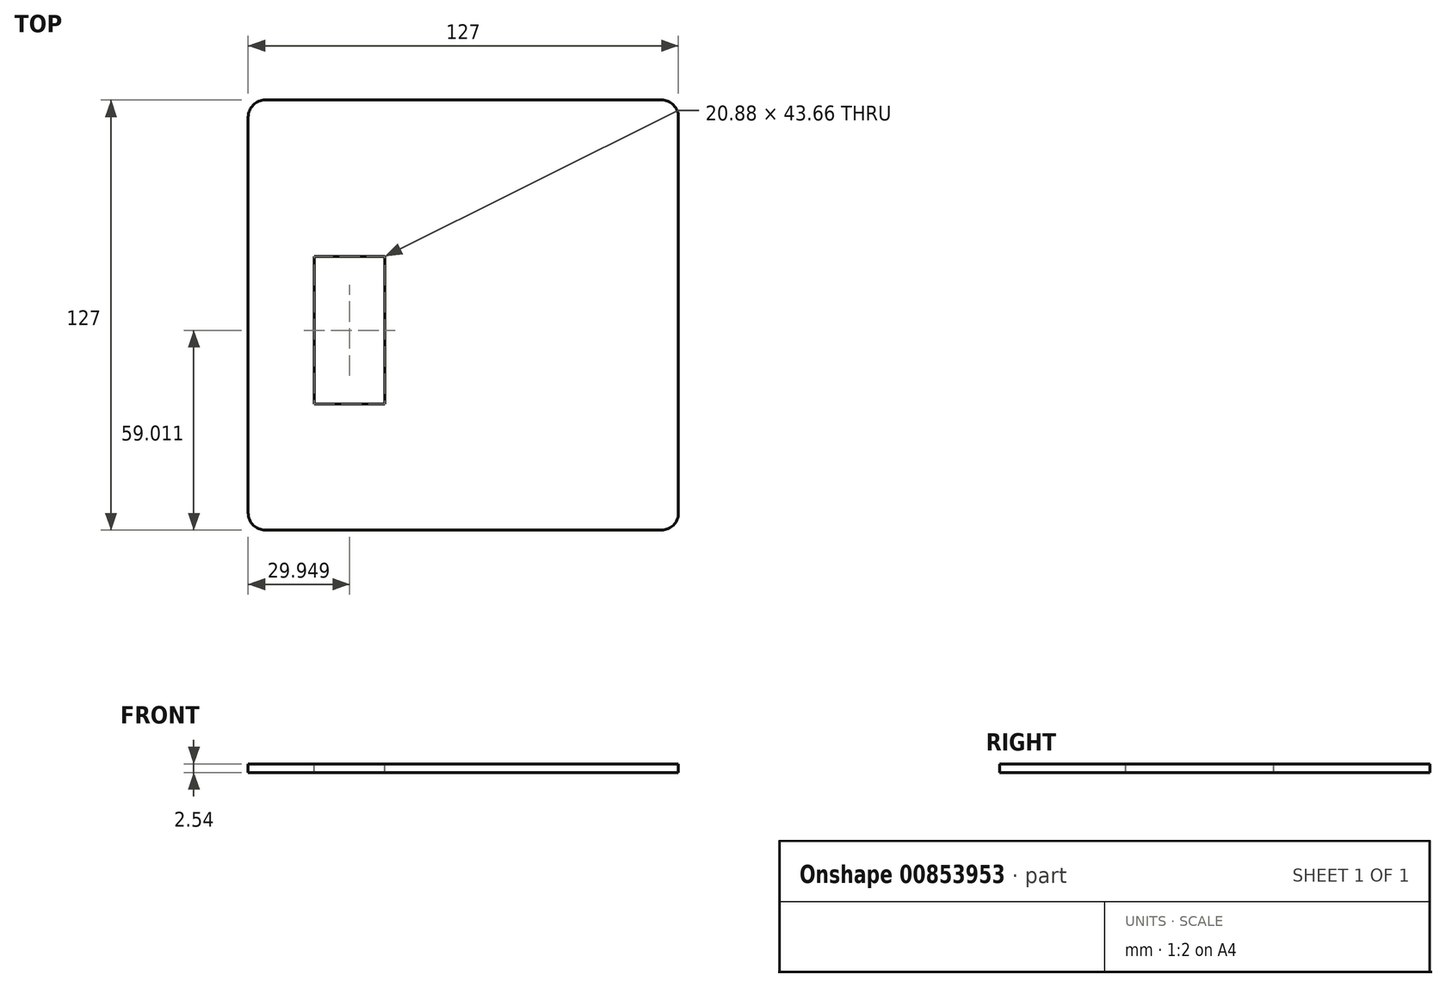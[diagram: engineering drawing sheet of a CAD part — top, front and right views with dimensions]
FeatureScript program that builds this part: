
annotation { "Feature Type Name" : "Feature", "Feature Type Description" : "" }
export const myFeature = defineFeature(function(context is Context, id is Id, definition is map)
    precondition{}
    {
        {
            var Q0;
            Q0=qCreatedBy(makeId("Top.planeOp"),FACE);
            var sketch = newSketch(context, id + "F0", { "sketchPlane" : qUnion([Q0])});
            skLineSegment(sketch, "E0.bottom", {"start": v(63.5, 63.5) * mm, "end": v(-63.5, 63.5) * mm});
            skLineSegment(sketch, "E0.top", {"start": v(63.5, -63.5) * mm, "end": v(-63.5, -63.5) * mm});
            skLineSegment(sketch, "E0.left", {"start": v(63.5, 63.5) * mm, "end": v(63.5, -63.5) * mm});
            skLineSegment(sketch, "E0.right", {"start": v(-63.5, 63.5) * mm, "end": v(-63.5, -63.5) * mm});
            skPoint(sketch, "E0.middle", {"position": v(0, 0) * mm});
            skSolve(sketch);
        }
        {
            var Q0;
            Q0=makeQuery(id+"F0.imprint","IMPRINT",FACE,{"disambiguationData":[TD([[makeQuery(id+"F0.imprint","IMPRINT",EDGE,{"derivedFrom":sQuery(id+"F0.wireOp",EDGE,"E0.bottom")}),1.0]])]});
            extrude(context, id + "F1", {"entities" : qUnion([Q0]), "depth" : 2.54 * mm, "offsetDistance" : 25.4 * mm});
        }
        {
            var Q0;
            Q0=makeQuery(id+"F1.opExtrude","SWEPT_EDGE",EDGE,{"disambiguationData":[OSD([sQuery(id+"F0.wireOp",EDGE,"E0.top"),sQuery(id+"F0.wireOp",EDGE,"E0.left")])]});
            var Q1;
            Q1=makeQuery(id+"F1.opExtrude","SWEPT_EDGE",EDGE,{"disambiguationData":[OSD([sQuery(id+"F0.wireOp",EDGE,"E0.bottom"),sQuery(id+"F0.wireOp",EDGE,"E0.left")])]});
            var Q2;
            Q2=makeQuery(id+"F1.opExtrude","SWEPT_EDGE",EDGE,{"disambiguationData":[OSD([sQuery(id+"F0.wireOp",EDGE,"E0.bottom"),sQuery(id+"F0.wireOp",EDGE,"E0.right")])]});
            var Q3;
            Q3=makeQuery(id+"F1.opExtrude","SWEPT_EDGE",EDGE,{"disambiguationData":[OSD([sQuery(id+"F0.wireOp",EDGE,"E0.top"),sQuery(id+"F0.wireOp",EDGE,"E0.right")])]});
            fillet(context, id + "F2", {"entities" : qUnion([Q0, Q1, Q2, Q3]), "radius" : 5.08 * mm, "tangentPropagation" : true, "allowEdgeOverflow" : false});
        }
        {
            var Q0;
            Q0=makeQuery(id+"F1.opExtrude","CAP_FACE",FACE,{"disambiguationData":[OSD([sQuery(id+"F0.wireOp",EDGE,"E0.bottom"),sQuery(id+"F0.wireOp",EDGE,"E0.top"),sQuery(id+"F0.wireOp",EDGE,"E0.left"),sQuery(id+"F0.wireOp",EDGE,"E0.right")])],"isStart":false});
            var sketch = newSketch(context, id + "F3", { "sketchPlane" : qUnion([Q0])});
            skLineSegment(sketch, "E1.bottom", {"start": v(-44, -26.32) * mm, "end": v(-23.1, -26.32) * mm});
            skLineSegment(sketch, "E1.top", {"start": v(-44, 17.34) * mm, "end": v(-23.1, 17.34) * mm});
            skLineSegment(sketch, "E1.left", {"start": v(-44, -26.32) * mm, "end": v(-44, 17.34) * mm});
            skLineSegment(sketch, "E1.right", {"start": v(-23.1, -26.32) * mm, "end": v(-23.1, 17.34) * mm});
            skSolve(sketch);
        }
        {
            var Q0;
            Q0=makeQuery(id+"F3.imprint","IMPRINT",FACE,{"disambiguationData":[TD([[makeQuery(id+"F3.imprint","IMPRINT",EDGE,{"derivedFrom":sQuery(id+"F3.wireOp",EDGE,"E1.bottom")}),1.0]])]});
            extrude(context, id + "F4", {"entities" : qUnion([Q0]), "operationType" : NewBodyOperationType.REMOVE, "oppositeDirection" : true, "depth" : 25.4 * mm, "offsetDistance" : 25.4 * mm});
        }
    });
